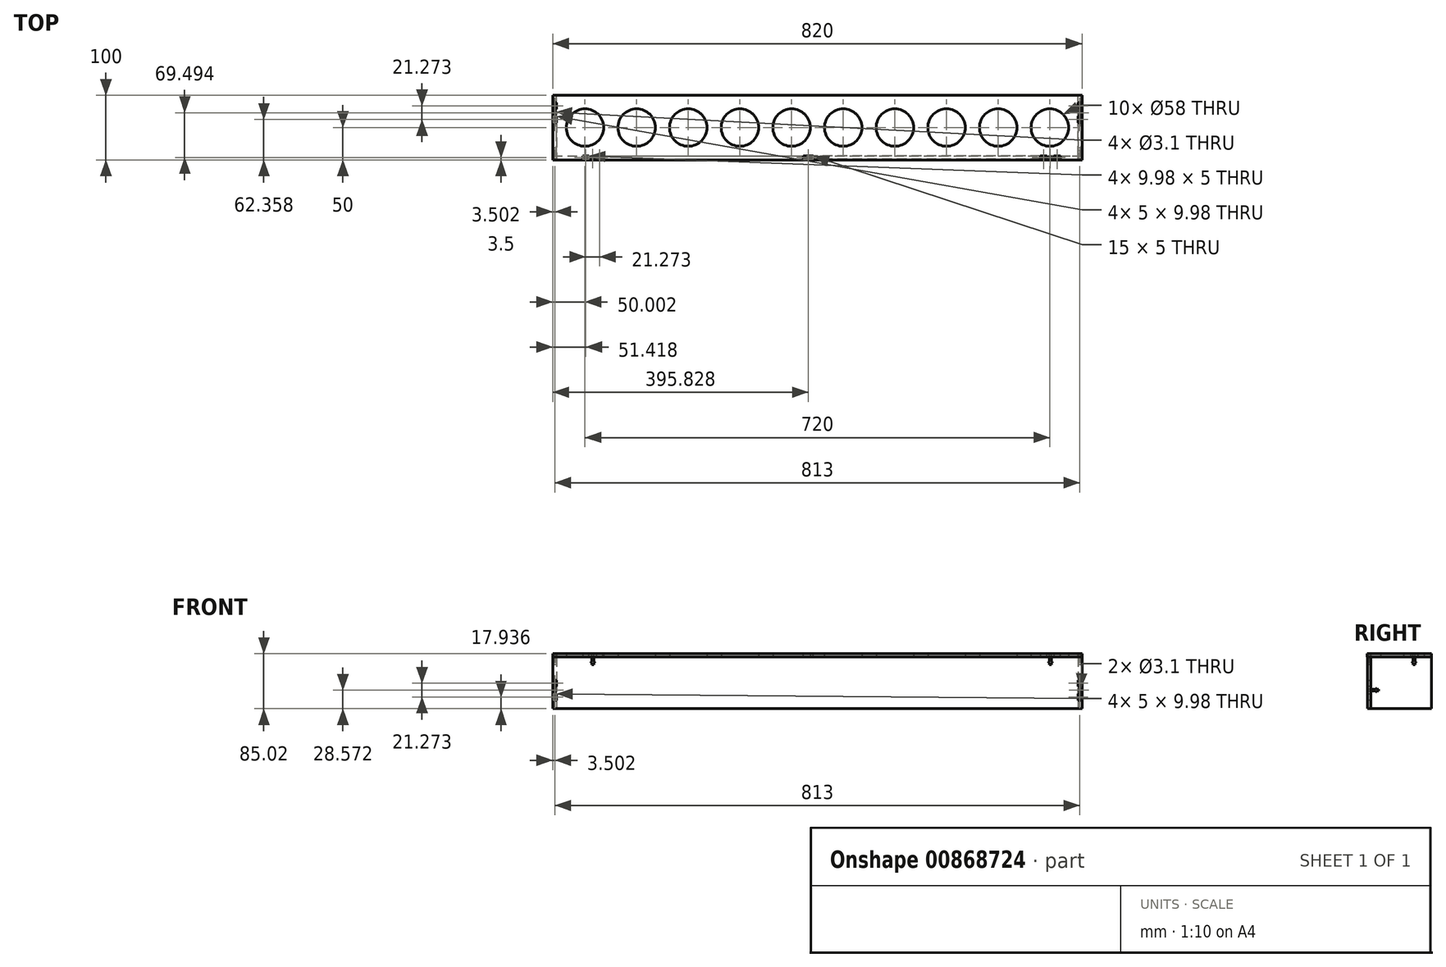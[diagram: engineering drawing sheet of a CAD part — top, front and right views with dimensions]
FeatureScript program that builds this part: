
annotation { "Feature Type Name" : "Feature", "Feature Type Description" : "" }
export const myFeature = defineFeature(function(context is Context, id is Id, definition is map)
    precondition{}
    {
        {
            var Q0;
            Q0=qCreatedBy(makeId("Top.planeOp"),FACE);
            var sketch = newSketch(context, id + "F0", { "sketchPlane" : qUnion([Q0])});
            skCircle(sketch, "E0", {"center": v(-73.63, 0) * mm, "radius": 29 * mm});
            skCircle(sketch, "E1", {"center": v(-73.63, 0) * mm, "radius": 40 * mm, "construction": true});
            skCircle(sketch, "E2.1.0.0", {"center": v(6.37, 0) * mm, "radius": 40 * mm, "construction": true});
            skCircle(sketch, "E2.1.0.1", {"center": v(6.37, 0) * mm, "radius": 29 * mm});
            skCircle(sketch, "E2.2.0.0", {"center": v(86.37, 0) * mm, "radius": 40 * mm, "construction": true});
            skCircle(sketch, "E2.2.0.1", {"center": v(86.37, 0) * mm, "radius": 29 * mm});
            skCircle(sketch, "E2.3.0.0", {"center": v(166.37, 0) * mm, "radius": 40 * mm, "construction": true});
            skCircle(sketch, "E2.3.0.1", {"center": v(166.37, 0) * mm, "radius": 29 * mm});
            skCircle(sketch, "E2.4.0.0", {"center": v(246.37, 0) * mm, "radius": 40 * mm, "construction": true});
            skCircle(sketch, "E2.4.0.1", {"center": v(246.37, 0) * mm, "radius": 29 * mm});
            skCircle(sketch, "E2.5.0.0", {"center": v(326.37, 0) * mm, "radius": 40 * mm, "construction": true});
            skCircle(sketch, "E2.5.0.1", {"center": v(326.37, 0) * mm, "radius": 29 * mm});
            skCircle(sketch, "E2.6.0.0", {"center": v(406.37, 0) * mm, "radius": 40 * mm, "construction": true});
            skCircle(sketch, "E2.6.0.1", {"center": v(406.37, 0) * mm, "radius": 29 * mm});
            skCircle(sketch, "E2.7.0.0", {"center": v(486.37, 0) * mm, "radius": 40 * mm, "construction": true});
            skCircle(sketch, "E2.7.0.1", {"center": v(486.37, 0) * mm, "radius": 29 * mm});
            skCircle(sketch, "E2.8.0.0", {"center": v(566.37, 0) * mm, "radius": 40 * mm, "construction": true});
            skCircle(sketch, "E2.8.0.1", {"center": v(566.37, 0) * mm, "radius": 29 * mm});
            skCircle(sketch, "E2.9.0.0", {"center": v(646.37, 0) * mm, "radius": 40 * mm, "construction": true});
            skCircle(sketch, "E2.9.0.1", {"center": v(646.37, 0) * mm, "radius": 29 * mm});
            skLineSegment(sketch, "E2.direction1", {"start": v(-73.63, 0) * mm, "end": v(6.37, 0) * mm, "construction": true});
            skLineSegment(sketch, "E3.bottom", {"start": v(-123.63, 50) * mm, "end": v(696.37, 50) * mm});
            skLineSegment(sketch, "E3.top", {"start": v(-123.63, -50) * mm, "end": v(696.37, -50) * mm});
            skLineSegment(sketch, "E3.left", {"start": v(-123.63, 50) * mm, "end": v(-123.63, -50) * mm});
            skLineSegment(sketch, "E3.right", {"start": v(696.37, 50) * mm, "end": v(696.37, -50) * mm});
            skSolve(sketch);
        }
        {
            var Q0;
            Q0 = qSketchRegion(id + "F0", true);
            extrude(context, id + "F1", {"entities" : qUnion([Q0]), "depth" : 5 * mm, "offsetDistance" : 25 * mm});
        }
        {
            var Q0;
            Q0=makeQuery(id+"F1.opExtrude","SWEPT_FACE",FACE,{"disambiguationData":[OSD([sQuery(id+"F0.wireOp",EDGE,"E3.top")])]});
            cPlane(context, id + "F2", {"entities" : qUnion([Q0]), "cplaneType" : CPlaneType.OFFSET, "offset" : 1 * mm, "oppositeDirection" : true, "width" : 150 * mm, "height" : 150 * mm});
        }
        {
            var Q0;
            Q0=qCreatedBy(id+"F2.planeOp",FACE);
            var sketch = newSketch(context, id + "F3", { "sketchPlane" : qUnion([Q0])});
            skPoint(sketch, "E4.0", {"position": v(-123.63, 0) * mm});
            skPoint(sketch, "E4.1", {"position": v(696.37, 0) * mm});
            skLineSegment(sketch, "E5.bottom", {"start": v(-123.63, 0) * mm, "end": v(-63.02, 0) * mm});
            skLineSegment(sketch, "E5.top", {"start": v(-123.63, -80) * mm, "end": v(696.37, -80) * mm});
            skLineSegment(sketch, "E5.left", {"start": v(-123.63, 0) * mm, "end": v(-123.63, -80) * mm});
            skLineSegment(sketch, "E5.right", {"start": v(696.37, 0) * mm, "end": v(696.37, -80) * mm});
            skLineSegment(sketch, "E6.trimOffspring", {"start": v(-28.43, 0) * mm, "end": v(264.7, 0) * mm});
            skLineSegment(sketch, "E7.trimOffspring", {"start": v(631.57, 0) * mm, "end": v(645.75, 0) * mm});
            skLineSegment(sketch, "E8.top", {"start": v(264.7, 5) * mm, "end": v(279.7, 5) * mm});
            skLineSegment(sketch, "E8.left", {"start": v(264.7, 0) * mm, "end": v(264.7, 5) * mm});
            skLineSegment(sketch, "E8.right", {"start": v(279.7, 0) * mm, "end": v(279.7, 5) * mm});
            skPoint(sketch, "E9.orphan", {"position": v(-123.63, 5) * mm});
            skLineSegment(sketch, "E10", {"start": v(631.57, 0) * mm, "end": v(279.7, 0) * mm});
            skLineSegment(sketch, "E11", {"start": v(662.83, 0) * mm, "end": v(662.83, 5.02) * mm});
            skLineSegment(sketch, "E12", {"start": v(662.83, 5.02) * mm, "end": v(652.84, 5.02) * mm});
            skLineSegment(sketch, "E13", {"start": v(652.84, 5.02) * mm, "end": v(652.84, 0) * mm});
            skLineSegment(sketch, "E14", {"start": v(652.84, 0) * mm, "end": v(648.65, 0) * mm});
            skLineSegment(sketch, "E15", {"start": v(648.65, 0) * mm, "end": v(648.65, -7.4) * mm});
            skLineSegment(sketch, "E16", {"start": v(648.65, -7.4) * mm, "end": v(649.9, -7.4) * mm});
            skLineSegment(sketch, "E17", {"start": v(649.9, -7.4) * mm, "end": v(649.9, -9.04) * mm});
            skLineSegment(sketch, "E18", {"start": v(649.9, -9.04) * mm, "end": v(648.65, -9.04) * mm});
            skLineSegment(sketch, "E19", {"start": v(648.65, -9.04) * mm, "end": v(648.65, -11.92) * mm});
            skLineSegment(sketch, "E20", {"start": v(648.65, -11.92) * mm, "end": v(645.75, -11.92) * mm});
            skLineSegment(sketch, "E21", {"start": v(645.75, -11.92) * mm, "end": v(645.75, -9.04) * mm});
            skLineSegment(sketch, "E22", {"start": v(645.75, -9.04) * mm, "end": v(644.5, -9.04) * mm});
            skLineSegment(sketch, "E23", {"start": v(644.5, -9.04) * mm, "end": v(644.5, -7.4) * mm});
            skLineSegment(sketch, "E24", {"start": v(644.5, -7.4) * mm, "end": v(645.75, -7.4) * mm});
            skLineSegment(sketch, "E25", {"start": v(645.75, -7.4) * mm, "end": v(645.75, 0) * mm});
            skLineSegment(sketch, "E26", {"start": v(645.75, 0) * mm, "end": v(641.56, 0) * mm});
            skLineSegment(sketch, "E27", {"start": v(641.56, 0) * mm, "end": v(641.56, 5.02) * mm});
            skLineSegment(sketch, "E28", {"start": v(641.56, 5.02) * mm, "end": v(631.57, 5.02) * mm});
            skLineSegment(sketch, "E29", {"start": v(631.57, 5.02) * mm, "end": v(631.57, 0) * mm});
            skLineSegment(sketch, "E30.trimOffspring", {"start": v(641.56, 0) * mm, "end": v(645.75, 0) * mm});
            skLineSegment(sketch, "E31.trimOffspring", {"start": v(648.65, 0) * mm, "end": v(652.84, 0) * mm});
            skLineSegment(sketch, "E32", {"start": v(-53.63, 0) * mm, "end": v(-28.43, 0) * mm});
            skLineSegment(sketch, "E33", {"start": v(-45.95, 0) * mm, "end": v(-45.95, 5.02) * mm});
            skLineSegment(sketch, "E34", {"start": v(-45.95, 5.02) * mm, "end": v(-55.93, 5.02) * mm});
            skLineSegment(sketch, "E35", {"start": v(-55.93, 5.02) * mm, "end": v(-55.93, 0) * mm});
            skLineSegment(sketch, "E36", {"start": v(-55.93, 0) * mm, "end": v(-60.13, 0) * mm});
            skLineSegment(sketch, "E37", {"start": v(-60.13, 0) * mm, "end": v(-60.13, -7.4) * mm});
            skLineSegment(sketch, "E38", {"start": v(-60.13, -7.4) * mm, "end": v(-58.87, -7.4) * mm});
            skLineSegment(sketch, "E39", {"start": v(-58.87, -7.4) * mm, "end": v(-58.87, -9.04) * mm});
            skLineSegment(sketch, "E40", {"start": v(-58.87, -9.04) * mm, "end": v(-60.13, -9.04) * mm});
            skLineSegment(sketch, "E41", {"start": v(-60.13, -9.04) * mm, "end": v(-60.13, -11.92) * mm});
            skLineSegment(sketch, "E42", {"start": v(-60.13, -11.92) * mm, "end": v(-63.02, -11.92) * mm});
            skLineSegment(sketch, "E43", {"start": v(-63.02, -11.92) * mm, "end": v(-63.02, -9.04) * mm});
            skLineSegment(sketch, "E44", {"start": v(-63.02, -9.04) * mm, "end": v(-64.28, -9.04) * mm});
            skLineSegment(sketch, "E45", {"start": v(-64.28, -9.04) * mm, "end": v(-64.28, -7.4) * mm});
            skLineSegment(sketch, "E46", {"start": v(-64.28, -7.4) * mm, "end": v(-63.02, -7.4) * mm});
            skLineSegment(sketch, "E47", {"start": v(-63.02, -7.4) * mm, "end": v(-63.02, 0) * mm});
            skLineSegment(sketch, "E48", {"start": v(-63.02, 0) * mm, "end": v(-67.22, 0) * mm});
            skLineSegment(sketch, "E49", {"start": v(-67.22, 0) * mm, "end": v(-67.22, 5.02) * mm});
            skLineSegment(sketch, "E50", {"start": v(-67.22, 5.02) * mm, "end": v(-77.2, 5.02) * mm});
            skLineSegment(sketch, "E51", {"start": v(-77.2, 5.02) * mm, "end": v(-77.2, 0) * mm});
            skLineSegment(sketch, "E52.trimOffspring", {"start": v(-67.22, 0) * mm, "end": v(-63.02, 0) * mm});
            skLineSegment(sketch, "E53.trimOffspring", {"start": v(-60.13, 0) * mm, "end": v(-55.93, 0) * mm});
            skLineSegment(sketch, "E54.trimOffspring", {"start": v(-60.13, 0) * mm, "end": v(-53.63, 0) * mm});
            skLineSegment(sketch, "E55.trimOffspring", {"start": v(648.65, 0) * mm, "end": v(696.37, 0) * mm});
            skSolve(sketch);
        }
        {
            var Q0;
            Q0 = qSketchRegion(id + "F3", true);
            extrude(context, id + "F4", {"entities" : qUnion([Q0]), "oppositeDirection" : true, "depth" : 5 * mm, "offsetDistance" : 25 * mm});
        }
        {
            var Q0;
            Q0=makeQuery(id+"F4.opExtrude","SWEPT_BODY",BODY,{"disambiguationData":[OSD([sQuery(id+"F3.wireOp",EDGE,"E5.bottom"),sQuery(id+"F3.wireOp",EDGE,"E5.top"),sQuery(id+"F3.wireOp",EDGE,"E5.left"),sQuery(id+"F3.wireOp",EDGE,"E5.right"),sQuery(id+"F3.wireOp",EDGE,"c6427b70-bbd1-47a5-9da8-1868f66dd3e5.bottom"),sQuery(id+"F3.wireOp",EDGE,"c6427b70-bbd1-47a5-9da8-1868f66dd3e5.top"),sQuery(id+"F3.wireOp",EDGE,"c6427b70-bbd1-47a5-9da8-1868f66dd3e5.right"),sQuery(id+"F3.wireOp",EDGE,"34134450-8dd6-4184-a5a5-a6bf2f12c070.bottom"),sQuery(id+"F3.wireOp",EDGE,"34134450-8dd6-4184-a5a5-a6bf2f12c070.top"),sQuery(id+"F3.wireOp",EDGE,"34134450-8dd6-4184-a5a5-a6bf2f12c070.left"),sQuery(id+"F3.wireOp",EDGE,"34134450-8dd6-4184-a5a5-a6bf2f12c070.right"),sQuery(id+"F3.wireOp",EDGE,"736ffd29-46f9-47cf-ae9a-fff26240e6ef.trimOffspring"),sQuery(id+"F3.wireOp",EDGE,"6e1e06c4-eae8-434f-a495-d8d1c42b03d7.trimOffspring"),sQuery(id+"F3.wireOp",EDGE,"095cc7c0-4786-4b79-9a77-49ee265b8b08.trimOffspring"),sQuery(id+"F3.wireOp",EDGE,"82320eba-51a6-4599-82f3-c4e99392a0c9.trimOffspring"),sQuery(id+"F3.wireOp",EDGE,"3cc5d4e1-7d26-4493-ae7c-d2b2cb5d12b6.bottom"),sQuery(id+"F3.wireOp",EDGE,"3cc5d4e1-7d26-4493-ae7c-d2b2cb5d12b6.top"),sQuery(id+"F3.wireOp",EDGE,"3cc5d4e1-7d26-4493-ae7c-d2b2cb5d12b6.right"),sQuery(id+"F3.wireOp",EDGE,"43e66698-d644-4a3e-a2a9-537bda9cd984.bottom"),sQuery(id+"F3.wireOp",EDGE,"43e66698-d644-4a3e-a2a9-537bda9cd984.top"),sQuery(id+"F3.wireOp",EDGE,"43e66698-d644-4a3e-a2a9-537bda9cd984.left"),sQuery(id+"F3.wireOp",EDGE,"43e66698-d644-4a3e-a2a9-537bda9cd984.right"),sQuery(id+"F3.wireOp",EDGE,"99af37e3-b37a-4aeb-bc7b-7b0e8f6b89a5.trimOffspring"),sQuery(id+"F3.wireOp",EDGE,"770e025a-9a19-494d-b11d-61fdc952efbf.trimOffspring"),sQuery(id+"F3.wireOp",EDGE,"91943c4e-1da0-40ed-9895-6108da8bfd9d.trimOffspring"),sQuery(id+"F3.wireOp",EDGE,"6429d018-5506-4dae-a2c4-f0ff895a1e2b.trimOffspring"),sQuery(id+"F3.wireOp",EDGE,"E6.trimOffspring"),sQuery(id+"F3.wireOp",EDGE,"E7.trimOffspring"),sQuery(id+"F3.wireOp",EDGE,"E8.left"),sQuery(id+"F3.wireOp",EDGE,"E8.right"),sQuery(id+"F3.wireOp",EDGE,"s4xGuCOs-RhxD-yV60-JvKa-MQL4linQS2L2.top"),sQuery(id+"F3.wireOp",EDGE,"s4xGuCOs-RhxD-yV60-JvKa-MQL4linQS2L2.left"),sQuery(id+"F3.wireOp",EDGE,"s4xGuCOs-RhxD-yV60-JvKa-MQL4linQS2L2.right"),sQuery(id+"F3.wireOp",EDGE,"O3syxvkP-Jdfe-WaZs-cZ3O-Vzp3Uvl644wq.left"),sQuery(id+"F3.wireOp",EDGE,"O3syxvkP-Jdfe-WaZs-cZ3O-Vzp3Uvl644wq.right"),sQuery(id+"F3.wireOp",EDGE,"lpcf8c3F-Q5bh-Wanz-ZhPp-yOcRjp1v02T7.left"),sQuery(id+"F3.wireOp",EDGE,"lpcf8c3F-Q5bh-Wanz-ZhPp-yOcRjp1v02T7.right"),sQuery(id+"F3.wireOp",EDGE,"OdtPCENa-pfhU-fLa5-guDU-6DtaNxlk325l.left"),sQuery(id+"F3.wireOp",EDGE,"OdtPCENa-pfhU-fLa5-guDU-6DtaNxlk325l.right"),sQuery(id+"F3.wireOp",EDGE,"fb442577-35d4-48bd-9fb2-5a3f11b94096.trimOffspring"),sQuery(id+"F3.wireOp",EDGE,"E8.top"),sQuery(id+"F3.wireOp",EDGE,"384e82a3-1d6c-40a9-a865-ccbdd03cb81e.trimOffspring"),sQuery(id+"F3.wireOp",EDGE,"172c6a1d-fd44-49c7-be3c-bc2e90b2fe12.trimOffspring"),sQuery(id+"F3.wireOp",EDGE,"431d8783-c629-4159-a5c0-239945ec4a9b.trimOffspring")])]});
            var Q1;
            Q1=makeQuery(id+"F1.opExtrude","SWEPT_BODY",BODY,{"disambiguationData":[OSD([sQuery(id+"F0.wireOp",EDGE,"E0"),sQuery(id+"F0.wireOp",EDGE,"E2.1.0.1"),sQuery(id+"F0.wireOp",EDGE,"E2.2.0.1"),sQuery(id+"F0.wireOp",EDGE,"E2.3.0.1"),sQuery(id+"F0.wireOp",EDGE,"E2.4.0.1"),sQuery(id+"F0.wireOp",EDGE,"E2.5.0.1"),sQuery(id+"F0.wireOp",EDGE,"E2.6.0.1"),sQuery(id+"F0.wireOp",EDGE,"E2.7.0.1"),sQuery(id+"F0.wireOp",EDGE,"E2.8.0.1"),sQuery(id+"F0.wireOp",EDGE,"E2.9.0.1"),sQuery(id+"F0.wireOp",EDGE,"E3.bottom"),sQuery(id+"F0.wireOp",EDGE,"E3.top"),sQuery(id+"F0.wireOp",EDGE,"E3.left"),sQuery(id+"F0.wireOp",EDGE,"E3.right")])]});
            booleanBodies(context, id + "F5", {"operationType" : BooleanOperationType.SUBTRACTION, "tools" : qUnion([Q0]), "targets" : qUnion([Q1]), "keepTools" : true});
        }
        {
            var Q0;
            Q0=makeQuery(id+"F1.opExtrude","SWEPT_FACE",FACE,{"disambiguationData":[OSD([sQuery(id+"F0.wireOp",EDGE,"E3.left")])]});
            cPlane(context, id + "F6", {"entities" : qUnion([Q0]), "cplaneType" : CPlaneType.OFFSET, "offset" : 1 * mm, "oppositeDirection" : true, "width" : 150 * mm, "height" : 150 * mm});
        }
        {
            var Q0;
            Q0=qCreatedBy(id+"F6.planeOp",FACE);
            var sketch = newSketch(context, id + "F7", { "sketchPlane" : qUnion([Q0])});
            skLineSegment(sketch, "E56.0", {"start": v(-50, 0) * mm, "end": v(-27.24, 0) * mm, "construction": true});
            skLineSegment(sketch, "E57.top", {"start": v(44, -80) * mm, "end": v(-50, -80) * mm});
            skLineSegment(sketch, "E57.right", {"start": v(-50, 0) * mm, "end": v(-50, -80) * mm});
            skLineSegment(sketch, "E58.trimOffspring", {"start": v(-27.24, 0) * mm, "end": v(-50, 0) * mm});
            skLineSegment(sketch, "E59.trimOffspring", {"start": v(44, -66.6) * mm, "end": v(44, -80) * mm, "construction": true});
            skLineSegment(sketch, "E60.trimOffspring", {"start": v(44, -66.6) * mm, "end": v(44, -80) * mm});
            skLineSegment(sketch, "E61", {"start": v(-50, 0) * mm, "end": v(-24.44, 0) * mm});
            skLineSegment(sketch, "E62", {"start": v(44, 0) * mm, "end": v(44, -49.98) * mm});
            skLineSegment(sketch, "E63", {"start": v(-7.37, 0) * mm, "end": v(-7.37, 5.02) * mm});
            skLineSegment(sketch, "E64", {"start": v(-7.37, 5.02) * mm, "end": v(-17.35, 5.02) * mm});
            skLineSegment(sketch, "E65", {"start": v(-17.35, 5.02) * mm, "end": v(-17.35, 0) * mm});
            skLineSegment(sketch, "E66", {"start": v(-17.35, 0) * mm, "end": v(-21.55, 0) * mm});
            skLineSegment(sketch, "E67", {"start": v(-21.55, 0) * mm, "end": v(-21.55, -7.4) * mm});
            skLineSegment(sketch, "E68", {"start": v(-21.55, -7.4) * mm, "end": v(-20.29, -7.4) * mm});
            skLineSegment(sketch, "E69", {"start": v(-20.29, -7.4) * mm, "end": v(-20.29, -9.04) * mm});
            skLineSegment(sketch, "E70", {"start": v(-20.29, -9.04) * mm, "end": v(-21.55, -9.04) * mm});
            skLineSegment(sketch, "E71", {"start": v(-21.55, -9.04) * mm, "end": v(-21.55, -11.92) * mm});
            skLineSegment(sketch, "E72", {"start": v(-21.55, -11.92) * mm, "end": v(-24.44, -11.92) * mm});
            skLineSegment(sketch, "E73", {"start": v(-24.44, -11.92) * mm, "end": v(-24.44, -9.04) * mm});
            skLineSegment(sketch, "E74", {"start": v(-24.44, -9.04) * mm, "end": v(-25.7, -9.04) * mm});
            skLineSegment(sketch, "E75", {"start": v(-25.7, -9.04) * mm, "end": v(-25.7, -7.4) * mm});
            skLineSegment(sketch, "E76", {"start": v(-25.7, -7.4) * mm, "end": v(-24.44, -7.4) * mm});
            skLineSegment(sketch, "E77", {"start": v(-24.44, -7.4) * mm, "end": v(-24.44, 0) * mm});
            skLineSegment(sketch, "E78", {"start": v(-24.44, 0) * mm, "end": v(-28.64, 0) * mm});
            skLineSegment(sketch, "E79", {"start": v(-28.64, 0) * mm, "end": v(-28.64, 5.02) * mm});
            skLineSegment(sketch, "E80", {"start": v(-28.64, 5.02) * mm, "end": v(-38.62, 5.02) * mm});
            skLineSegment(sketch, "E81", {"start": v(-38.62, 5.02) * mm, "end": v(-38.62, 0) * mm});
            skLineSegment(sketch, "E82.trimOffspring", {"start": v(-28.64, 0) * mm, "end": v(-24.44, 0) * mm});
            skLineSegment(sketch, "E83.trimOffspring", {"start": v(-21.55, 0) * mm, "end": v(-17.35, 0) * mm});
            skLineSegment(sketch, "E84", {"start": v(44, -67.06) * mm, "end": v(49.02, -67.06) * mm});
            skLineSegment(sketch, "E85", {"start": v(49.02, -67.06) * mm, "end": v(49.02, -57.07) * mm});
            skLineSegment(sketch, "E86", {"start": v(49.02, -57.07) * mm, "end": v(44, -57.07) * mm});
            skLineSegment(sketch, "E87", {"start": v(44, -57.07) * mm, "end": v(44, -52.87) * mm});
            skLineSegment(sketch, "E88", {"start": v(44, -52.87) * mm, "end": v(36.6, -52.87) * mm});
            skLineSegment(sketch, "E89", {"start": v(36.6, -52.87) * mm, "end": v(36.6, -54.14) * mm});
            skLineSegment(sketch, "E90", {"start": v(36.6, -54.14) * mm, "end": v(34.96, -54.14) * mm});
            skLineSegment(sketch, "E91", {"start": v(34.96, -54.14) * mm, "end": v(34.96, -52.87) * mm});
            skLineSegment(sketch, "E92", {"start": v(34.96, -52.87) * mm, "end": v(32.08, -52.87) * mm});
            skLineSegment(sketch, "E93", {"start": v(32.08, -52.87) * mm, "end": v(32.08, -49.98) * mm});
            skLineSegment(sketch, "E94", {"start": v(32.08, -49.98) * mm, "end": v(34.96, -49.98) * mm});
            skLineSegment(sketch, "E95", {"start": v(34.96, -49.98) * mm, "end": v(34.96, -48.72) * mm});
            skLineSegment(sketch, "E96", {"start": v(34.96, -48.72) * mm, "end": v(36.6, -48.72) * mm});
            skLineSegment(sketch, "E97", {"start": v(36.6, -48.72) * mm, "end": v(36.6, -49.98) * mm});
            skLineSegment(sketch, "E98", {"start": v(36.6, -49.98) * mm, "end": v(44, -49.98) * mm});
            skLineSegment(sketch, "E99", {"start": v(44, -49.98) * mm, "end": v(44, -45.78) * mm});
            skLineSegment(sketch, "E100", {"start": v(44, -45.78) * mm, "end": v(49.02, -45.78) * mm});
            skLineSegment(sketch, "E101", {"start": v(49.02, -45.78) * mm, "end": v(49.02, -35.8) * mm});
            skLineSegment(sketch, "E102", {"start": v(49.02, -35.8) * mm, "end": v(44, -35.8) * mm});
            skLineSegment(sketch, "E103.trimOffspring", {"start": v(44, -45.78) * mm, "end": v(44, -49.98) * mm});
            skLineSegment(sketch, "E104.trimOffspring", {"start": v(44, -52.87) * mm, "end": v(44, -57.07) * mm});
            skLineSegment(sketch, "E105.trimOffspring", {"start": v(-21.55, 0) * mm, "end": v(44, 0) * mm});
            skLineSegment(sketch, "E106.trimOffspring", {"start": v(44, -52.87) * mm, "end": v(44, -80) * mm});
            skSolve(sketch);
        }
        {
            var Q0;
            Q0 = qSketchRegion(id + "F7", true);
            extrude(context, id + "F8", {"entities" : qUnion([Q0]), "oppositeDirection" : true, "depth" : 5 * mm, "offsetDistance" : 25 * mm});
        }
        {
            var Q0;
            Q0=makeQuery(id+"F8.opExtrude","SWEPT_BODY",BODY,{"disambiguationData":[OSD([sQuery(id+"F7.wireOp",EDGE,"E57.top"),sQuery(id+"F7.wireOp",EDGE,"E57.right"),sQuery(id+"F7.wireOp",EDGE,"E61"),sQuery(id+"F7.wireOp",EDGE,"E62"),sQuery(id+"F7.wireOp",EDGE,"E63"),sQuery(id+"F7.wireOp",EDGE,"E64"),sQuery(id+"F7.wireOp",EDGE,"E65"),sQuery(id+"F7.wireOp",EDGE,"E67"),sQuery(id+"F7.wireOp",EDGE,"E68"),sQuery(id+"F7.wireOp",EDGE,"E69"),sQuery(id+"F7.wireOp",EDGE,"E70"),sQuery(id+"F7.wireOp",EDGE,"E71"),sQuery(id+"F7.wireOp",EDGE,"E72"),sQuery(id+"F7.wireOp",EDGE,"E73"),sQuery(id+"F7.wireOp",EDGE,"E74"),sQuery(id+"F7.wireOp",EDGE,"E75"),sQuery(id+"F7.wireOp",EDGE,"E76"),sQuery(id+"F7.wireOp",EDGE,"E77"),sQuery(id+"F7.wireOp",EDGE,"E79"),sQuery(id+"F7.wireOp",EDGE,"E80"),sQuery(id+"F7.wireOp",EDGE,"E81"),sQuery(id+"F7.wireOp",EDGE,"E78"),sQuery(id+"F7.wireOp",EDGE,"E84"),sQuery(id+"F7.wireOp",EDGE,"E85"),sQuery(id+"F7.wireOp",EDGE,"E86"),sQuery(id+"F7.wireOp",EDGE,"E88"),sQuery(id+"F7.wireOp",EDGE,"E89"),sQuery(id+"F7.wireOp",EDGE,"E90"),sQuery(id+"F7.wireOp",EDGE,"E91"),sQuery(id+"F7.wireOp",EDGE,"E92"),sQuery(id+"F7.wireOp",EDGE,"E93"),sQuery(id+"F7.wireOp",EDGE,"E94"),sQuery(id+"F7.wireOp",EDGE,"E95"),sQuery(id+"F7.wireOp",EDGE,"E96"),sQuery(id+"F7.wireOp",EDGE,"E97"),sQuery(id+"F7.wireOp",EDGE,"E98"),sQuery(id+"F7.wireOp",EDGE,"E100"),sQuery(id+"F7.wireOp",EDGE,"E101"),sQuery(id+"F7.wireOp",EDGE,"E102"),sQuery(id+"F7.wireOp",EDGE,"E99"),sQuery(id+"F7.wireOp",EDGE,"E105.trimOffspring"),sQuery(id+"F7.wireOp",EDGE,"E106.trimOffspring")])]});
            transform(context, id + "F9", {"entities" : qUnion([Q0]), "transformType" : TransformType.TRANSLATION_3D, "dx" : 813 * mm, "dy" : 0 * mm, "dz" : 0 * mm, "makeCopy" : true});
        }
        {
            var Q0;
            Q0=makeQuery(id+"F9.opPattern","COPY",BODY,{"derivedFrom":makeQuery(id+"F8.opExtrude","SWEPT_BODY",BODY,{"disambiguationData":[OSD([sQuery(id+"F7.wireOp",EDGE,"E57.top"),sQuery(id+"F7.wireOp",EDGE,"E57.right"),sQuery(id+"F7.wireOp",EDGE,"E61"),sQuery(id+"F7.wireOp",EDGE,"E62"),sQuery(id+"F7.wireOp",EDGE,"E63"),sQuery(id+"F7.wireOp",EDGE,"E64"),sQuery(id+"F7.wireOp",EDGE,"E65"),sQuery(id+"F7.wireOp",EDGE,"E67"),sQuery(id+"F7.wireOp",EDGE,"E68"),sQuery(id+"F7.wireOp",EDGE,"E69"),sQuery(id+"F7.wireOp",EDGE,"E70"),sQuery(id+"F7.wireOp",EDGE,"E71"),sQuery(id+"F7.wireOp",EDGE,"E72"),sQuery(id+"F7.wireOp",EDGE,"E73"),sQuery(id+"F7.wireOp",EDGE,"E74"),sQuery(id+"F7.wireOp",EDGE,"E75"),sQuery(id+"F7.wireOp",EDGE,"E76"),sQuery(id+"F7.wireOp",EDGE,"E77"),sQuery(id+"F7.wireOp",EDGE,"E79"),sQuery(id+"F7.wireOp",EDGE,"E80"),sQuery(id+"F7.wireOp",EDGE,"E81"),sQuery(id+"F7.wireOp",EDGE,"E78"),sQuery(id+"F7.wireOp",EDGE,"E84"),sQuery(id+"F7.wireOp",EDGE,"E85"),sQuery(id+"F7.wireOp",EDGE,"E86"),sQuery(id+"F7.wireOp",EDGE,"E88"),sQuery(id+"F7.wireOp",EDGE,"E89"),sQuery(id+"F7.wireOp",EDGE,"E90"),sQuery(id+"F7.wireOp",EDGE,"E91"),sQuery(id+"F7.wireOp",EDGE,"E92"),sQuery(id+"F7.wireOp",EDGE,"E93"),sQuery(id+"F7.wireOp",EDGE,"E94"),sQuery(id+"F7.wireOp",EDGE,"E95"),sQuery(id+"F7.wireOp",EDGE,"E96"),sQuery(id+"F7.wireOp",EDGE,"E97"),sQuery(id+"F7.wireOp",EDGE,"E98"),sQuery(id+"F7.wireOp",EDGE,"E100"),sQuery(id+"F7.wireOp",EDGE,"E101"),sQuery(id+"F7.wireOp",EDGE,"E102"),sQuery(id+"F7.wireOp",EDGE,"E99"),sQuery(id+"F7.wireOp",EDGE,"E105.trimOffspring"),sQuery(id+"F7.wireOp",EDGE,"E106.trimOffspring")])]}),"instanceName":"1"});
            var Q1;
            Q1=makeQuery(id+"F8.opExtrude","SWEPT_BODY",BODY,{"disambiguationData":[OSD([sQuery(id+"F7.wireOp",EDGE,"E57.top"),sQuery(id+"F7.wireOp",EDGE,"E57.right"),sQuery(id+"F7.wireOp",EDGE,"E61"),sQuery(id+"F7.wireOp",EDGE,"E62"),sQuery(id+"F7.wireOp",EDGE,"E63"),sQuery(id+"F7.wireOp",EDGE,"E64"),sQuery(id+"F7.wireOp",EDGE,"E65"),sQuery(id+"F7.wireOp",EDGE,"E67"),sQuery(id+"F7.wireOp",EDGE,"E68"),sQuery(id+"F7.wireOp",EDGE,"E69"),sQuery(id+"F7.wireOp",EDGE,"E70"),sQuery(id+"F7.wireOp",EDGE,"E71"),sQuery(id+"F7.wireOp",EDGE,"E72"),sQuery(id+"F7.wireOp",EDGE,"E73"),sQuery(id+"F7.wireOp",EDGE,"E74"),sQuery(id+"F7.wireOp",EDGE,"E75"),sQuery(id+"F7.wireOp",EDGE,"E76"),sQuery(id+"F7.wireOp",EDGE,"E77"),sQuery(id+"F7.wireOp",EDGE,"E79"),sQuery(id+"F7.wireOp",EDGE,"E80"),sQuery(id+"F7.wireOp",EDGE,"E81"),sQuery(id+"F7.wireOp",EDGE,"E78"),sQuery(id+"F7.wireOp",EDGE,"E84"),sQuery(id+"F7.wireOp",EDGE,"E85"),sQuery(id+"F7.wireOp",EDGE,"E86"),sQuery(id+"F7.wireOp",EDGE,"E88"),sQuery(id+"F7.wireOp",EDGE,"E89"),sQuery(id+"F7.wireOp",EDGE,"E90"),sQuery(id+"F7.wireOp",EDGE,"E91"),sQuery(id+"F7.wireOp",EDGE,"E92"),sQuery(id+"F7.wireOp",EDGE,"E93"),sQuery(id+"F7.wireOp",EDGE,"E94"),sQuery(id+"F7.wireOp",EDGE,"E95"),sQuery(id+"F7.wireOp",EDGE,"E96"),sQuery(id+"F7.wireOp",EDGE,"E97"),sQuery(id+"F7.wireOp",EDGE,"E98"),sQuery(id+"F7.wireOp",EDGE,"E100"),sQuery(id+"F7.wireOp",EDGE,"E101"),sQuery(id+"F7.wireOp",EDGE,"E102"),sQuery(id+"F7.wireOp",EDGE,"E99"),sQuery(id+"F7.wireOp",EDGE,"E105.trimOffspring"),sQuery(id+"F7.wireOp",EDGE,"E106.trimOffspring")])]});
            var Q2;
            Q2=makeQuery(id+"F1.opExtrude","SWEPT_BODY",BODY,{"disambiguationData":[OSD([sQuery(id+"F0.wireOp",EDGE,"E0"),sQuery(id+"F0.wireOp",EDGE,"E2.1.0.1"),sQuery(id+"F0.wireOp",EDGE,"E2.2.0.1"),sQuery(id+"F0.wireOp",EDGE,"E2.3.0.1"),sQuery(id+"F0.wireOp",EDGE,"E2.4.0.1"),sQuery(id+"F0.wireOp",EDGE,"E2.5.0.1"),sQuery(id+"F0.wireOp",EDGE,"E2.6.0.1"),sQuery(id+"F0.wireOp",EDGE,"E2.7.0.1"),sQuery(id+"F0.wireOp",EDGE,"E2.8.0.1"),sQuery(id+"F0.wireOp",EDGE,"E2.9.0.1"),sQuery(id+"F0.wireOp",EDGE,"E3.bottom"),sQuery(id+"F0.wireOp",EDGE,"E3.top"),sQuery(id+"F0.wireOp",EDGE,"E3.left"),sQuery(id+"F0.wireOp",EDGE,"E3.right")])]});
            booleanBodies(context, id + "F10", {"operationType" : BooleanOperationType.SUBTRACTION, "tools" : qUnion([Q0, Q1]), "targets" : qUnion([Q2]), "keepTools" : true});
        }
        {
            var Q0;
            Q0=makeQuery(id+"F1.opExtrude","CAP_FACE",FACE,{"disambiguationData":[OSD([sQuery(id+"F0.wireOp",EDGE,"E0"),sQuery(id+"F0.wireOp",EDGE,"E2.1.0.1"),sQuery(id+"F0.wireOp",EDGE,"E2.2.0.1"),sQuery(id+"F0.wireOp",EDGE,"E2.3.0.1"),sQuery(id+"F0.wireOp",EDGE,"E2.4.0.1"),sQuery(id+"F0.wireOp",EDGE,"E2.5.0.1"),sQuery(id+"F0.wireOp",EDGE,"E2.6.0.1"),sQuery(id+"F0.wireOp",EDGE,"E2.7.0.1"),sQuery(id+"F0.wireOp",EDGE,"E2.8.0.1"),sQuery(id+"F0.wireOp",EDGE,"E2.9.0.1"),sQuery(id+"F0.wireOp",EDGE,"E3.bottom"),sQuery(id+"F0.wireOp",EDGE,"E3.top"),sQuery(id+"F0.wireOp",EDGE,"E3.left"),sQuery(id+"F0.wireOp",EDGE,"E3.right")])],"isStart":false});
            var sketch = newSketch(context, id + "F11", { "sketchPlane" : qUnion([Q0])});
            skLineSegment(sketch, "E107.0", {"start": v(-67.22, -44) * mm, "end": v(-67.22, -49) * mm, "construction": true});
            skLineSegment(sketch, "E107.1", {"start": v(-55.93, -44) * mm, "end": v(-55.93, -49) * mm, "construction": true});
            skLineSegment(sketch, "E107.2", {"start": v(-117.63, 28.64) * mm, "end": v(-122.63, 28.64) * mm, "construction": true});
            skLineSegment(sketch, "E107.3", {"start": v(-117.63, 17.35) * mm, "end": v(-122.63, 17.35) * mm, "construction": true});
            skLineSegment(sketch, "E107.4", {"start": v(652.84, -44) * mm, "end": v(652.84, -49) * mm, "construction": true});
            skLineSegment(sketch, "E107.5", {"start": v(641.56, -44) * mm, "end": v(641.56, -49) * mm, "construction": true});
            skLineSegment(sketch, "E107.6", {"start": v(695.37, 17.35) * mm, "end": v(690.37, 17.35) * mm, "construction": true});
            skLineSegment(sketch, "E107.7", {"start": v(695.37, 28.64) * mm, "end": v(690.37, 28.64) * mm, "construction": true});
            skLineSegment(sketch, "E108", {"start": v(-120.13, 28.64) * mm, "end": v(-120.13, 17.35) * mm, "construction": true});
            skLineSegment(sketch, "E109", {"start": v(-67.22, -46.5) * mm, "end": v(-55.93, -46.5) * mm, "construction": true});
            skLineSegment(sketch, "E110", {"start": v(641.56, -46.5) * mm, "end": v(652.84, -46.5) * mm, "construction": true});
            skLineSegment(sketch, "E111", {"start": v(692.87, 28.64) * mm, "end": v(692.87, 17.35) * mm, "construction": true});
            skPoint(sketch, "E112", {"position": v(647.2, -46.5) * mm});
            skPoint(sketch, "E113", {"position": v(692.87, 23) * mm});
            skPoint(sketch, "E114", {"position": v(-61.58, -46.5) * mm});
            skPoint(sketch, "E115", {"position": v(-120.13, 23) * mm});
            skSolve(sketch);
        }
        {
            var Q0;
            Q0=sQuery(id+"F11.wireOp",VERTEX,"E115");
            var Q1;
            Q1=sQuery(id+"F11.wireOp",VERTEX,"E114");
            var Q2;
            Q2=sQuery(id+"F11.wireOp",VERTEX,"E113");
            var Q3;
            Q3=sQuery(id+"F11.wireOp",VERTEX,"E112");
            var Q4;
            Q4=makeQuery(id+"F1.opExtrude","SWEPT_BODY",BODY,{"disambiguationData":[OSD([sQuery(id+"F0.wireOp",EDGE,"E0"),sQuery(id+"F0.wireOp",EDGE,"E2.1.0.1"),sQuery(id+"F0.wireOp",EDGE,"E2.2.0.1"),sQuery(id+"F0.wireOp",EDGE,"E2.3.0.1"),sQuery(id+"F0.wireOp",EDGE,"E2.4.0.1"),sQuery(id+"F0.wireOp",EDGE,"E2.5.0.1"),sQuery(id+"F0.wireOp",EDGE,"E2.6.0.1"),sQuery(id+"F0.wireOp",EDGE,"E2.7.0.1"),sQuery(id+"F0.wireOp",EDGE,"E2.8.0.1"),sQuery(id+"F0.wireOp",EDGE,"E2.9.0.1"),sQuery(id+"F0.wireOp",EDGE,"E3.bottom"),sQuery(id+"F0.wireOp",EDGE,"E3.top"),sQuery(id+"F0.wireOp",EDGE,"E3.left"),sQuery(id+"F0.wireOp",EDGE,"E3.right")])]});
            var Q5;
            Q5=makeQuery(id+"F8.opExtrude","SWEPT_BODY",BODY,{"disambiguationData":[OSD([sQuery(id+"F7.wireOp",EDGE,"E57.top"),sQuery(id+"F7.wireOp",EDGE,"E57.right"),sQuery(id+"F7.wireOp",EDGE,"E61"),sQuery(id+"F7.wireOp",EDGE,"E62"),sQuery(id+"F7.wireOp",EDGE,"E63"),sQuery(id+"F7.wireOp",EDGE,"E64"),sQuery(id+"F7.wireOp",EDGE,"E65"),sQuery(id+"F7.wireOp",EDGE,"E67"),sQuery(id+"F7.wireOp",EDGE,"E68"),sQuery(id+"F7.wireOp",EDGE,"E69"),sQuery(id+"F7.wireOp",EDGE,"E70"),sQuery(id+"F7.wireOp",EDGE,"E71"),sQuery(id+"F7.wireOp",EDGE,"E72"),sQuery(id+"F7.wireOp",EDGE,"E73"),sQuery(id+"F7.wireOp",EDGE,"E74"),sQuery(id+"F7.wireOp",EDGE,"E75"),sQuery(id+"F7.wireOp",EDGE,"E76"),sQuery(id+"F7.wireOp",EDGE,"E77"),sQuery(id+"F7.wireOp",EDGE,"E79"),sQuery(id+"F7.wireOp",EDGE,"E80"),sQuery(id+"F7.wireOp",EDGE,"E81"),sQuery(id+"F7.wireOp",EDGE,"E78"),sQuery(id+"F7.wireOp",EDGE,"E84"),sQuery(id+"F7.wireOp",EDGE,"E85"),sQuery(id+"F7.wireOp",EDGE,"E86"),sQuery(id+"F7.wireOp",EDGE,"E88"),sQuery(id+"F7.wireOp",EDGE,"E89"),sQuery(id+"F7.wireOp",EDGE,"E90"),sQuery(id+"F7.wireOp",EDGE,"E91"),sQuery(id+"F7.wireOp",EDGE,"E92"),sQuery(id+"F7.wireOp",EDGE,"E93"),sQuery(id+"F7.wireOp",EDGE,"E94"),sQuery(id+"F7.wireOp",EDGE,"E95"),sQuery(id+"F7.wireOp",EDGE,"E96"),sQuery(id+"F7.wireOp",EDGE,"E97"),sQuery(id+"F7.wireOp",EDGE,"E98"),sQuery(id+"F7.wireOp",EDGE,"E100"),sQuery(id+"F7.wireOp",EDGE,"E101"),sQuery(id+"F7.wireOp",EDGE,"E102"),sQuery(id+"F7.wireOp",EDGE,"E99"),sQuery(id+"F7.wireOp",EDGE,"E105.trimOffspring"),sQuery(id+"F7.wireOp",EDGE,"E106.trimOffspring")])]});
            var Q6;
            Q6=makeQuery(id+"F4.opExtrude","SWEPT_BODY",BODY,{"disambiguationData":[OSD([sQuery(id+"F3.wireOp",EDGE,"E5.bottom"),sQuery(id+"F3.wireOp",EDGE,"E5.top"),sQuery(id+"F3.wireOp",EDGE,"E5.left"),sQuery(id+"F3.wireOp",EDGE,"E5.right"),sQuery(id+"F3.wireOp",EDGE,"E6.trimOffspring"),sQuery(id+"F3.wireOp",EDGE,"E8.left"),sQuery(id+"F3.wireOp",EDGE,"E8.right"),sQuery(id+"F3.wireOp",EDGE,"E8.top"),sQuery(id+"F3.wireOp",EDGE,"E10"),sQuery(id+"F3.wireOp",EDGE,"E11"),sQuery(id+"F3.wireOp",EDGE,"E12"),sQuery(id+"F3.wireOp",EDGE,"E13"),sQuery(id+"F3.wireOp",EDGE,"E15"),sQuery(id+"F3.wireOp",EDGE,"E16"),sQuery(id+"F3.wireOp",EDGE,"E17"),sQuery(id+"F3.wireOp",EDGE,"E18"),sQuery(id+"F3.wireOp",EDGE,"E19"),sQuery(id+"F3.wireOp",EDGE,"E20"),sQuery(id+"F3.wireOp",EDGE,"E21"),sQuery(id+"F3.wireOp",EDGE,"E22"),sQuery(id+"F3.wireOp",EDGE,"E23"),sQuery(id+"F3.wireOp",EDGE,"E24"),sQuery(id+"F3.wireOp",EDGE,"E25"),sQuery(id+"F3.wireOp",EDGE,"E27"),sQuery(id+"F3.wireOp",EDGE,"E28"),sQuery(id+"F3.wireOp",EDGE,"E29"),sQuery(id+"F3.wireOp",EDGE,"E26"),sQuery(id+"F3.wireOp",EDGE,"E32"),sQuery(id+"F3.wireOp",EDGE,"E33"),sQuery(id+"F3.wireOp",EDGE,"E34"),sQuery(id+"F3.wireOp",EDGE,"E35"),sQuery(id+"F3.wireOp",EDGE,"E37"),sQuery(id+"F3.wireOp",EDGE,"E38"),sQuery(id+"F3.wireOp",EDGE,"E39"),sQuery(id+"F3.wireOp",EDGE,"E40"),sQuery(id+"F3.wireOp",EDGE,"E41"),sQuery(id+"F3.wireOp",EDGE,"E42"),sQuery(id+"F3.wireOp",EDGE,"E43"),sQuery(id+"F3.wireOp",EDGE,"E44"),sQuery(id+"F3.wireOp",EDGE,"E45"),sQuery(id+"F3.wireOp",EDGE,"E46"),sQuery(id+"F3.wireOp",EDGE,"E47"),sQuery(id+"F3.wireOp",EDGE,"E49"),sQuery(id+"F3.wireOp",EDGE,"E50"),sQuery(id+"F3.wireOp",EDGE,"E51"),sQuery(id+"F3.wireOp",EDGE,"E48"),sQuery(id+"F3.wireOp",EDGE,"E54.trimOffspring"),sQuery(id+"F3.wireOp",EDGE,"E55.trimOffspring")])]});
            var Q7;
            Q7=makeQuery(id+"F9.opPattern","COPY",BODY,{"derivedFrom":makeQuery(id+"F8.opExtrude","SWEPT_BODY",BODY,{"disambiguationData":[OSD([sQuery(id+"F7.wireOp",EDGE,"E57.top"),sQuery(id+"F7.wireOp",EDGE,"E57.right"),sQuery(id+"F7.wireOp",EDGE,"E61"),sQuery(id+"F7.wireOp",EDGE,"E62"),sQuery(id+"F7.wireOp",EDGE,"E63"),sQuery(id+"F7.wireOp",EDGE,"E64"),sQuery(id+"F7.wireOp",EDGE,"E65"),sQuery(id+"F7.wireOp",EDGE,"E67"),sQuery(id+"F7.wireOp",EDGE,"E68"),sQuery(id+"F7.wireOp",EDGE,"E69"),sQuery(id+"F7.wireOp",EDGE,"E70"),sQuery(id+"F7.wireOp",EDGE,"E71"),sQuery(id+"F7.wireOp",EDGE,"E72"),sQuery(id+"F7.wireOp",EDGE,"E73"),sQuery(id+"F7.wireOp",EDGE,"E74"),sQuery(id+"F7.wireOp",EDGE,"E75"),sQuery(id+"F7.wireOp",EDGE,"E76"),sQuery(id+"F7.wireOp",EDGE,"E77"),sQuery(id+"F7.wireOp",EDGE,"E79"),sQuery(id+"F7.wireOp",EDGE,"E80"),sQuery(id+"F7.wireOp",EDGE,"E81"),sQuery(id+"F7.wireOp",EDGE,"E78"),sQuery(id+"F7.wireOp",EDGE,"E84"),sQuery(id+"F7.wireOp",EDGE,"E85"),sQuery(id+"F7.wireOp",EDGE,"E86"),sQuery(id+"F7.wireOp",EDGE,"E88"),sQuery(id+"F7.wireOp",EDGE,"E89"),sQuery(id+"F7.wireOp",EDGE,"E90"),sQuery(id+"F7.wireOp",EDGE,"E91"),sQuery(id+"F7.wireOp",EDGE,"E92"),sQuery(id+"F7.wireOp",EDGE,"E93"),sQuery(id+"F7.wireOp",EDGE,"E94"),sQuery(id+"F7.wireOp",EDGE,"E95"),sQuery(id+"F7.wireOp",EDGE,"E96"),sQuery(id+"F7.wireOp",EDGE,"E97"),sQuery(id+"F7.wireOp",EDGE,"E98"),sQuery(id+"F7.wireOp",EDGE,"E100"),sQuery(id+"F7.wireOp",EDGE,"E101"),sQuery(id+"F7.wireOp",EDGE,"E102"),sQuery(id+"F7.wireOp",EDGE,"E99"),sQuery(id+"F7.wireOp",EDGE,"E105.trimOffspring"),sQuery(id+"F7.wireOp",EDGE,"E106.trimOffspring")])]}),"instanceName":"1"});
            hole(context, id + "F12", {"style" : HoleStyle.SIMPLE, "endStyle" : HoleEndStyle.BLIND, "holeDiameter" : 3.1 * mm, "majorDiameter" : 5 * mm, "holeDepth" : 12 * mm, "isTappedThrough" : true, "tappedDepth" : 12 * mm, "tapClearance" : 3, "locations" : qUnion([Q0, Q1, Q2, Q3]), "scope" : qUnion([Q4, Q5, Q6, Q7])});
        }
        {
            var Q0;
            Q0=makeQuery(id+"F4.opExtrude","CAP_FACE",FACE,{"disambiguationData":[OSD([sQuery(id+"F3.wireOp",EDGE,"E5.bottom"),sQuery(id+"F3.wireOp",EDGE,"E5.top"),sQuery(id+"F3.wireOp",EDGE,"E5.left"),sQuery(id+"F3.wireOp",EDGE,"E5.right"),sQuery(id+"F3.wireOp",EDGE,"E6.trimOffspring"),sQuery(id+"F3.wireOp",EDGE,"E8.left"),sQuery(id+"F3.wireOp",EDGE,"E8.right"),sQuery(id+"F3.wireOp",EDGE,"E8.top"),sQuery(id+"F3.wireOp",EDGE,"E10"),sQuery(id+"F3.wireOp",EDGE,"E11"),sQuery(id+"F3.wireOp",EDGE,"E12"),sQuery(id+"F3.wireOp",EDGE,"E13"),sQuery(id+"F3.wireOp",EDGE,"E15"),sQuery(id+"F3.wireOp",EDGE,"E16"),sQuery(id+"F3.wireOp",EDGE,"E17"),sQuery(id+"F3.wireOp",EDGE,"E18"),sQuery(id+"F3.wireOp",EDGE,"E19"),sQuery(id+"F3.wireOp",EDGE,"E20"),sQuery(id+"F3.wireOp",EDGE,"E21"),sQuery(id+"F3.wireOp",EDGE,"E22"),sQuery(id+"F3.wireOp",EDGE,"E23"),sQuery(id+"F3.wireOp",EDGE,"E24"),sQuery(id+"F3.wireOp",EDGE,"E25"),sQuery(id+"F3.wireOp",EDGE,"E27"),sQuery(id+"F3.wireOp",EDGE,"E28"),sQuery(id+"F3.wireOp",EDGE,"E29"),sQuery(id+"F3.wireOp",EDGE,"E26"),sQuery(id+"F3.wireOp",EDGE,"E32"),sQuery(id+"F3.wireOp",EDGE,"E33"),sQuery(id+"F3.wireOp",EDGE,"E34"),sQuery(id+"F3.wireOp",EDGE,"E35"),sQuery(id+"F3.wireOp",EDGE,"E37"),sQuery(id+"F3.wireOp",EDGE,"E38"),sQuery(id+"F3.wireOp",EDGE,"E39"),sQuery(id+"F3.wireOp",EDGE,"E40"),sQuery(id+"F3.wireOp",EDGE,"E41"),sQuery(id+"F3.wireOp",EDGE,"E42"),sQuery(id+"F3.wireOp",EDGE,"E43"),sQuery(id+"F3.wireOp",EDGE,"E44"),sQuery(id+"F3.wireOp",EDGE,"E45"),sQuery(id+"F3.wireOp",EDGE,"E46"),sQuery(id+"F3.wireOp",EDGE,"E47"),sQuery(id+"F3.wireOp",EDGE,"E49"),sQuery(id+"F3.wireOp",EDGE,"E50"),sQuery(id+"F3.wireOp",EDGE,"E51"),sQuery(id+"F3.wireOp",EDGE,"E48"),sQuery(id+"F3.wireOp",EDGE,"E54.trimOffspring"),sQuery(id+"F3.wireOp",EDGE,"E55.trimOffspring")])],"isStart":true});
            var sketch = newSketch(context, id + "F13", { "sketchPlane" : qUnion([Q0])});
            skLineSegment(sketch, "E116.0", {"start": v(695.37, -45.78) * mm, "end": v(690.37, -45.78) * mm, "construction": true});
            skLineSegment(sketch, "E116.1", {"start": v(695.37, -57.07) * mm, "end": v(690.37, -57.07) * mm, "construction": true});
            skLineSegment(sketch, "E116.2", {"start": v(-117.63, -45.78) * mm, "end": v(-122.63, -45.78) * mm, "construction": true});
            skLineSegment(sketch, "E116.3", {"start": v(-117.63, -57.07) * mm, "end": v(-122.63, -57.07) * mm, "construction": true});
            skLineSegment(sketch, "E117", {"start": v(-120.13, -45.78) * mm, "end": v(-120.13, -57.07) * mm, "construction": true});
            skLineSegment(sketch, "E118", {"start": v(692.87, -45.78) * mm, "end": v(692.87, -57.07) * mm, "construction": true});
            skPoint(sketch, "E119", {"position": v(692.87, -51.43) * mm});
            skPoint(sketch, "E120", {"position": v(-120.13, -51.43) * mm});
            skSolve(sketch);
        }
        {
            var Q0;
            Q0=sQuery(id+"F13.wireOp",VERTEX,"E120");
            var Q1;
            Q1=sQuery(id+"F13.wireOp",VERTEX,"E119");
            var Q2;
            Q2=makeQuery(id+"F8.opExtrude","SWEPT_BODY",BODY,{"disambiguationData":[OSD([sQuery(id+"F7.wireOp",EDGE,"E57.top"),sQuery(id+"F7.wireOp",EDGE,"E57.right"),sQuery(id+"F7.wireOp",EDGE,"E61"),sQuery(id+"F7.wireOp",EDGE,"E62"),sQuery(id+"F7.wireOp",EDGE,"E63"),sQuery(id+"F7.wireOp",EDGE,"E64"),sQuery(id+"F7.wireOp",EDGE,"E65"),sQuery(id+"F7.wireOp",EDGE,"E67"),sQuery(id+"F7.wireOp",EDGE,"E68"),sQuery(id+"F7.wireOp",EDGE,"E69"),sQuery(id+"F7.wireOp",EDGE,"E70"),sQuery(id+"F7.wireOp",EDGE,"E71"),sQuery(id+"F7.wireOp",EDGE,"E72"),sQuery(id+"F7.wireOp",EDGE,"E73"),sQuery(id+"F7.wireOp",EDGE,"E74"),sQuery(id+"F7.wireOp",EDGE,"E75"),sQuery(id+"F7.wireOp",EDGE,"E76"),sQuery(id+"F7.wireOp",EDGE,"E77"),sQuery(id+"F7.wireOp",EDGE,"E79"),sQuery(id+"F7.wireOp",EDGE,"E80"),sQuery(id+"F7.wireOp",EDGE,"E81"),sQuery(id+"F7.wireOp",EDGE,"E78"),sQuery(id+"F7.wireOp",EDGE,"E84"),sQuery(id+"F7.wireOp",EDGE,"E85"),sQuery(id+"F7.wireOp",EDGE,"E86"),sQuery(id+"F7.wireOp",EDGE,"E88"),sQuery(id+"F7.wireOp",EDGE,"E89"),sQuery(id+"F7.wireOp",EDGE,"E90"),sQuery(id+"F7.wireOp",EDGE,"E91"),sQuery(id+"F7.wireOp",EDGE,"E92"),sQuery(id+"F7.wireOp",EDGE,"E93"),sQuery(id+"F7.wireOp",EDGE,"E94"),sQuery(id+"F7.wireOp",EDGE,"E95"),sQuery(id+"F7.wireOp",EDGE,"E96"),sQuery(id+"F7.wireOp",EDGE,"E97"),sQuery(id+"F7.wireOp",EDGE,"E98"),sQuery(id+"F7.wireOp",EDGE,"E100"),sQuery(id+"F7.wireOp",EDGE,"E101"),sQuery(id+"F7.wireOp",EDGE,"E102"),sQuery(id+"F7.wireOp",EDGE,"E99"),sQuery(id+"F7.wireOp",EDGE,"E105.trimOffspring"),sQuery(id+"F7.wireOp",EDGE,"E106.trimOffspring")])]});
            var Q3;
            Q3=makeQuery(id+"F4.opExtrude","SWEPT_BODY",BODY,{"disambiguationData":[OSD([sQuery(id+"F3.wireOp",EDGE,"E5.bottom"),sQuery(id+"F3.wireOp",EDGE,"E5.top"),sQuery(id+"F3.wireOp",EDGE,"E5.left"),sQuery(id+"F3.wireOp",EDGE,"E5.right"),sQuery(id+"F3.wireOp",EDGE,"E6.trimOffspring"),sQuery(id+"F3.wireOp",EDGE,"E8.left"),sQuery(id+"F3.wireOp",EDGE,"E8.right"),sQuery(id+"F3.wireOp",EDGE,"E8.top"),sQuery(id+"F3.wireOp",EDGE,"E10"),sQuery(id+"F3.wireOp",EDGE,"E11"),sQuery(id+"F3.wireOp",EDGE,"E12"),sQuery(id+"F3.wireOp",EDGE,"E13"),sQuery(id+"F3.wireOp",EDGE,"E15"),sQuery(id+"F3.wireOp",EDGE,"E16"),sQuery(id+"F3.wireOp",EDGE,"E17"),sQuery(id+"F3.wireOp",EDGE,"E18"),sQuery(id+"F3.wireOp",EDGE,"E19"),sQuery(id+"F3.wireOp",EDGE,"E20"),sQuery(id+"F3.wireOp",EDGE,"E21"),sQuery(id+"F3.wireOp",EDGE,"E22"),sQuery(id+"F3.wireOp",EDGE,"E23"),sQuery(id+"F3.wireOp",EDGE,"E24"),sQuery(id+"F3.wireOp",EDGE,"E25"),sQuery(id+"F3.wireOp",EDGE,"E27"),sQuery(id+"F3.wireOp",EDGE,"E28"),sQuery(id+"F3.wireOp",EDGE,"E29"),sQuery(id+"F3.wireOp",EDGE,"E26"),sQuery(id+"F3.wireOp",EDGE,"E32"),sQuery(id+"F3.wireOp",EDGE,"E33"),sQuery(id+"F3.wireOp",EDGE,"E34"),sQuery(id+"F3.wireOp",EDGE,"E35"),sQuery(id+"F3.wireOp",EDGE,"E37"),sQuery(id+"F3.wireOp",EDGE,"E38"),sQuery(id+"F3.wireOp",EDGE,"E39"),sQuery(id+"F3.wireOp",EDGE,"E40"),sQuery(id+"F3.wireOp",EDGE,"E41"),sQuery(id+"F3.wireOp",EDGE,"E42"),sQuery(id+"F3.wireOp",EDGE,"E43"),sQuery(id+"F3.wireOp",EDGE,"E44"),sQuery(id+"F3.wireOp",EDGE,"E45"),sQuery(id+"F3.wireOp",EDGE,"E46"),sQuery(id+"F3.wireOp",EDGE,"E47"),sQuery(id+"F3.wireOp",EDGE,"E49"),sQuery(id+"F3.wireOp",EDGE,"E50"),sQuery(id+"F3.wireOp",EDGE,"E51"),sQuery(id+"F3.wireOp",EDGE,"E48"),sQuery(id+"F3.wireOp",EDGE,"E54.trimOffspring"),sQuery(id+"F3.wireOp",EDGE,"E55.trimOffspring")])]});
            var Q4;
            Q4=makeQuery(id+"F9.opPattern","COPY",BODY,{"derivedFrom":makeQuery(id+"F8.opExtrude","SWEPT_BODY",BODY,{"disambiguationData":[OSD([sQuery(id+"F7.wireOp",EDGE,"E57.top"),sQuery(id+"F7.wireOp",EDGE,"E57.right"),sQuery(id+"F7.wireOp",EDGE,"E61"),sQuery(id+"F7.wireOp",EDGE,"E62"),sQuery(id+"F7.wireOp",EDGE,"E63"),sQuery(id+"F7.wireOp",EDGE,"E64"),sQuery(id+"F7.wireOp",EDGE,"E65"),sQuery(id+"F7.wireOp",EDGE,"E67"),sQuery(id+"F7.wireOp",EDGE,"E68"),sQuery(id+"F7.wireOp",EDGE,"E69"),sQuery(id+"F7.wireOp",EDGE,"E70"),sQuery(id+"F7.wireOp",EDGE,"E71"),sQuery(id+"F7.wireOp",EDGE,"E72"),sQuery(id+"F7.wireOp",EDGE,"E73"),sQuery(id+"F7.wireOp",EDGE,"E74"),sQuery(id+"F7.wireOp",EDGE,"E75"),sQuery(id+"F7.wireOp",EDGE,"E76"),sQuery(id+"F7.wireOp",EDGE,"E77"),sQuery(id+"F7.wireOp",EDGE,"E79"),sQuery(id+"F7.wireOp",EDGE,"E80"),sQuery(id+"F7.wireOp",EDGE,"E81"),sQuery(id+"F7.wireOp",EDGE,"E78"),sQuery(id+"F7.wireOp",EDGE,"E84"),sQuery(id+"F7.wireOp",EDGE,"E85"),sQuery(id+"F7.wireOp",EDGE,"E86"),sQuery(id+"F7.wireOp",EDGE,"E88"),sQuery(id+"F7.wireOp",EDGE,"E89"),sQuery(id+"F7.wireOp",EDGE,"E90"),sQuery(id+"F7.wireOp",EDGE,"E91"),sQuery(id+"F7.wireOp",EDGE,"E92"),sQuery(id+"F7.wireOp",EDGE,"E93"),sQuery(id+"F7.wireOp",EDGE,"E94"),sQuery(id+"F7.wireOp",EDGE,"E95"),sQuery(id+"F7.wireOp",EDGE,"E96"),sQuery(id+"F7.wireOp",EDGE,"E97"),sQuery(id+"F7.wireOp",EDGE,"E98"),sQuery(id+"F7.wireOp",EDGE,"E100"),sQuery(id+"F7.wireOp",EDGE,"E101"),sQuery(id+"F7.wireOp",EDGE,"E102"),sQuery(id+"F7.wireOp",EDGE,"E99"),sQuery(id+"F7.wireOp",EDGE,"E105.trimOffspring"),sQuery(id+"F7.wireOp",EDGE,"E106.trimOffspring")])]}),"instanceName":"1"});
            hole(context, id + "F14", {"style" : HoleStyle.SIMPLE, "endStyle" : HoleEndStyle.BLIND, "holeDiameter" : 3.1 * mm, "majorDiameter" : 5 * mm, "holeDepth" : 12 * mm, "isTappedThrough" : true, "tappedDepth" : 12 * mm, "tapClearance" : 3, "locations" : qUnion([Q0, Q1]), "scope" : qUnion([Q2, Q3, Q4])});
        }
        {
            var Q0;
            Q0=makeQuery(id+"F9.opPattern","COPY",BODY,{"derivedFrom":makeQuery(id+"F8.opExtrude","SWEPT_BODY",BODY,{"disambiguationData":[OSD([sQuery(id+"F7.wireOp",EDGE,"E57.top"),sQuery(id+"F7.wireOp",EDGE,"E57.right"),sQuery(id+"F7.wireOp",EDGE,"E61"),sQuery(id+"F7.wireOp",EDGE,"E62"),sQuery(id+"F7.wireOp",EDGE,"E63"),sQuery(id+"F7.wireOp",EDGE,"E64"),sQuery(id+"F7.wireOp",EDGE,"E65"),sQuery(id+"F7.wireOp",EDGE,"E67"),sQuery(id+"F7.wireOp",EDGE,"E68"),sQuery(id+"F7.wireOp",EDGE,"E69"),sQuery(id+"F7.wireOp",EDGE,"E70"),sQuery(id+"F7.wireOp",EDGE,"E71"),sQuery(id+"F7.wireOp",EDGE,"E72"),sQuery(id+"F7.wireOp",EDGE,"E73"),sQuery(id+"F7.wireOp",EDGE,"E74"),sQuery(id+"F7.wireOp",EDGE,"E75"),sQuery(id+"F7.wireOp",EDGE,"E76"),sQuery(id+"F7.wireOp",EDGE,"E77"),sQuery(id+"F7.wireOp",EDGE,"E79"),sQuery(id+"F7.wireOp",EDGE,"E80"),sQuery(id+"F7.wireOp",EDGE,"E81"),sQuery(id+"F7.wireOp",EDGE,"E78"),sQuery(id+"F7.wireOp",EDGE,"E84"),sQuery(id+"F7.wireOp",EDGE,"E85"),sQuery(id+"F7.wireOp",EDGE,"E86"),sQuery(id+"F7.wireOp",EDGE,"E88"),sQuery(id+"F7.wireOp",EDGE,"E89"),sQuery(id+"F7.wireOp",EDGE,"E90"),sQuery(id+"F7.wireOp",EDGE,"E91"),sQuery(id+"F7.wireOp",EDGE,"E92"),sQuery(id+"F7.wireOp",EDGE,"E93"),sQuery(id+"F7.wireOp",EDGE,"E94"),sQuery(id+"F7.wireOp",EDGE,"E95"),sQuery(id+"F7.wireOp",EDGE,"E96"),sQuery(id+"F7.wireOp",EDGE,"E97"),sQuery(id+"F7.wireOp",EDGE,"E98"),sQuery(id+"F7.wireOp",EDGE,"E100"),sQuery(id+"F7.wireOp",EDGE,"E101"),sQuery(id+"F7.wireOp",EDGE,"E102"),sQuery(id+"F7.wireOp",EDGE,"E99"),sQuery(id+"F7.wireOp",EDGE,"E105.trimOffspring"),sQuery(id+"F7.wireOp",EDGE,"E106.trimOffspring")])]}),"instanceName":"1"});
            var Q1;
            Q1=makeQuery(id+"F8.opExtrude","SWEPT_BODY",BODY,{"disambiguationData":[OSD([sQuery(id+"F7.wireOp",EDGE,"E57.top"),sQuery(id+"F7.wireOp",EDGE,"E57.right"),sQuery(id+"F7.wireOp",EDGE,"E61"),sQuery(id+"F7.wireOp",EDGE,"E62"),sQuery(id+"F7.wireOp",EDGE,"E63"),sQuery(id+"F7.wireOp",EDGE,"E64"),sQuery(id+"F7.wireOp",EDGE,"E65"),sQuery(id+"F7.wireOp",EDGE,"E67"),sQuery(id+"F7.wireOp",EDGE,"E68"),sQuery(id+"F7.wireOp",EDGE,"E69"),sQuery(id+"F7.wireOp",EDGE,"E70"),sQuery(id+"F7.wireOp",EDGE,"E71"),sQuery(id+"F7.wireOp",EDGE,"E72"),sQuery(id+"F7.wireOp",EDGE,"E73"),sQuery(id+"F7.wireOp",EDGE,"E74"),sQuery(id+"F7.wireOp",EDGE,"E75"),sQuery(id+"F7.wireOp",EDGE,"E76"),sQuery(id+"F7.wireOp",EDGE,"E77"),sQuery(id+"F7.wireOp",EDGE,"E79"),sQuery(id+"F7.wireOp",EDGE,"E80"),sQuery(id+"F7.wireOp",EDGE,"E81"),sQuery(id+"F7.wireOp",EDGE,"E78"),sQuery(id+"F7.wireOp",EDGE,"E84"),sQuery(id+"F7.wireOp",EDGE,"E85"),sQuery(id+"F7.wireOp",EDGE,"E86"),sQuery(id+"F7.wireOp",EDGE,"E88"),sQuery(id+"F7.wireOp",EDGE,"E89"),sQuery(id+"F7.wireOp",EDGE,"E90"),sQuery(id+"F7.wireOp",EDGE,"E91"),sQuery(id+"F7.wireOp",EDGE,"E92"),sQuery(id+"F7.wireOp",EDGE,"E93"),sQuery(id+"F7.wireOp",EDGE,"E94"),sQuery(id+"F7.wireOp",EDGE,"E95"),sQuery(id+"F7.wireOp",EDGE,"E96"),sQuery(id+"F7.wireOp",EDGE,"E97"),sQuery(id+"F7.wireOp",EDGE,"E98"),sQuery(id+"F7.wireOp",EDGE,"E100"),sQuery(id+"F7.wireOp",EDGE,"E101"),sQuery(id+"F7.wireOp",EDGE,"E102"),sQuery(id+"F7.wireOp",EDGE,"E99"),sQuery(id+"F7.wireOp",EDGE,"E105.trimOffspring"),sQuery(id+"F7.wireOp",EDGE,"E106.trimOffspring")])]});
            var Q2;
            Q2=makeQuery(id+"F4.opExtrude","SWEPT_BODY",BODY,{"disambiguationData":[OSD([sQuery(id+"F3.wireOp",EDGE,"E5.bottom"),sQuery(id+"F3.wireOp",EDGE,"E5.top"),sQuery(id+"F3.wireOp",EDGE,"E5.left"),sQuery(id+"F3.wireOp",EDGE,"E5.right"),sQuery(id+"F3.wireOp",EDGE,"E6.trimOffspring"),sQuery(id+"F3.wireOp",EDGE,"E8.left"),sQuery(id+"F3.wireOp",EDGE,"E8.right"),sQuery(id+"F3.wireOp",EDGE,"E8.top"),sQuery(id+"F3.wireOp",EDGE,"E10"),sQuery(id+"F3.wireOp",EDGE,"E11"),sQuery(id+"F3.wireOp",EDGE,"E12"),sQuery(id+"F3.wireOp",EDGE,"E13"),sQuery(id+"F3.wireOp",EDGE,"E15"),sQuery(id+"F3.wireOp",EDGE,"E16"),sQuery(id+"F3.wireOp",EDGE,"E17"),sQuery(id+"F3.wireOp",EDGE,"E18"),sQuery(id+"F3.wireOp",EDGE,"E19"),sQuery(id+"F3.wireOp",EDGE,"E20"),sQuery(id+"F3.wireOp",EDGE,"E21"),sQuery(id+"F3.wireOp",EDGE,"E22"),sQuery(id+"F3.wireOp",EDGE,"E23"),sQuery(id+"F3.wireOp",EDGE,"E24"),sQuery(id+"F3.wireOp",EDGE,"E25"),sQuery(id+"F3.wireOp",EDGE,"E27"),sQuery(id+"F3.wireOp",EDGE,"E28"),sQuery(id+"F3.wireOp",EDGE,"E29"),sQuery(id+"F3.wireOp",EDGE,"E26"),sQuery(id+"F3.wireOp",EDGE,"E32"),sQuery(id+"F3.wireOp",EDGE,"E33"),sQuery(id+"F3.wireOp",EDGE,"E34"),sQuery(id+"F3.wireOp",EDGE,"E35"),sQuery(id+"F3.wireOp",EDGE,"E37"),sQuery(id+"F3.wireOp",EDGE,"E38"),sQuery(id+"F3.wireOp",EDGE,"E39"),sQuery(id+"F3.wireOp",EDGE,"E40"),sQuery(id+"F3.wireOp",EDGE,"E41"),sQuery(id+"F3.wireOp",EDGE,"E42"),sQuery(id+"F3.wireOp",EDGE,"E43"),sQuery(id+"F3.wireOp",EDGE,"E44"),sQuery(id+"F3.wireOp",EDGE,"E45"),sQuery(id+"F3.wireOp",EDGE,"E46"),sQuery(id+"F3.wireOp",EDGE,"E47"),sQuery(id+"F3.wireOp",EDGE,"E49"),sQuery(id+"F3.wireOp",EDGE,"E50"),sQuery(id+"F3.wireOp",EDGE,"E51"),sQuery(id+"F3.wireOp",EDGE,"E48"),sQuery(id+"F3.wireOp",EDGE,"E54.trimOffspring"),sQuery(id+"F3.wireOp",EDGE,"E55.trimOffspring")])]});
            booleanBodies(context, id + "F15", {"operationType" : BooleanOperationType.SUBTRACTION, "tools" : qUnion([Q0, Q1]), "targets" : qUnion([Q2]), "keepTools" : true});
        }
    });
